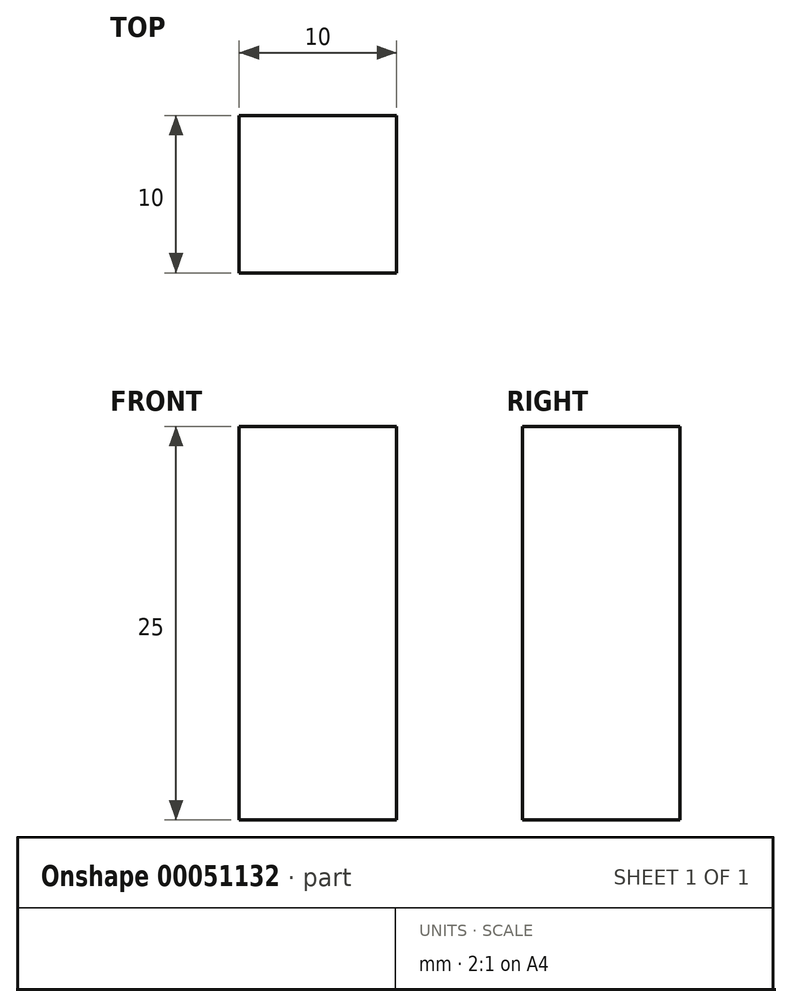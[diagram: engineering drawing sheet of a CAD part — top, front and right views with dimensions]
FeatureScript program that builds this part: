
annotation { "Feature Type Name" : "Feature", "Feature Type Description" : "" }
export const myFeature = defineFeature(function(context is Context, id is Id, definition is map)
    precondition{}
    {
        {
            var Q0;
            Q0=qCreatedBy(makeId("Top.planeOp"),FACE);
            var sketch = newSketch(context, id + "F0", { "sketchPlane" : qUnion([Q0])});
            skLineSegment(sketch, "E0.bottom", {"start": v(0, 0) * mm, "end": v(10, 0) * mm});
            skLineSegment(sketch, "E0.top", {"start": v(0, 10) * mm, "end": v(10, 10) * mm});
            skLineSegment(sketch, "E0.left", {"start": v(0, 0) * mm, "end": v(0, 10) * mm});
            skLineSegment(sketch, "E0.right", {"start": v(10, 0) * mm, "end": v(10, 10) * mm});
            skSolve(sketch);
        }
        {
            var Q0;
            Q0=makeQuery(id+"F0.imprint","IMPRINT",FACE,{"disambiguationData":[TD([[makeQuery(id+"F0.imprint","IMPRINT",EDGE,{"derivedFrom":sQuery(id+"F0.wireOp",EDGE,"E0.bottom")}),1.0]])]});
            extrude(context, id + "F1", {"entities" : qUnion([Q0]), "depth" : 25 * mm});
        }
    });
